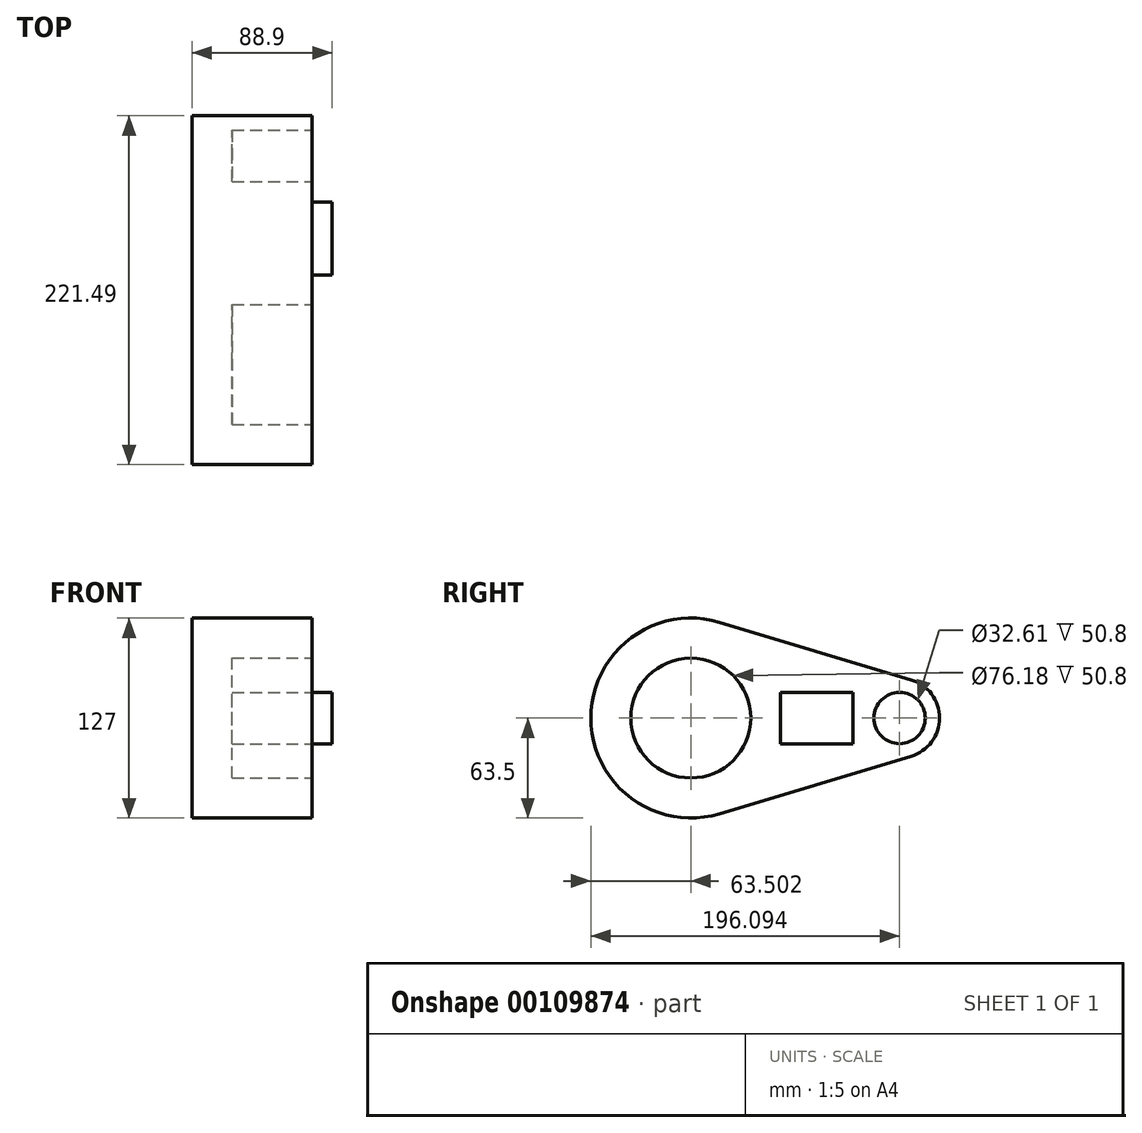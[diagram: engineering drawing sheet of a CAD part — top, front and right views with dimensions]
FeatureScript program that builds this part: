
annotation { "Feature Type Name" : "Feature", "Feature Type Description" : "" }
export const myFeature = defineFeature(function(context is Context, id is Id, definition is map)
    precondition{}
    {
        {
            var Q0;
            Q0=qCreatedBy(makeId("Right.planeOp"),FACE);
            var sketch = newSketch(context, id + "F0", { "sketchPlane" : qUnion([Q0])});
            skCircle(sketch, "E0", {"center": v(-79.97, 0) * mm, "radius": 63.5 * mm});
            skCircle(sketch, "E1", {"center": v(52.62, 0) * mm, "radius": 25.4 * mm});
            skLineSegment(sketch, "E2", {"start": v(-61.72, 60.82) * mm, "end": v(59.92, 24.33) * mm});
            skLineSegment(sketch, "E3", {"start": v(-61.72, -60.82) * mm, "end": v(59.92, -24.33) * mm});
            skSolve(sketch);
        }
        {
            var Q0;
            Q0 = qSketchRegion(id + "F0", true);
            extrude(context, id + "F1", {"entities" : qUnion([Q0]), "depth" : 76.2 * mm});
        }
        {
            var Q0;
            Q0=makeQuery(id+"F1.opExtrude","CAP_FACE",FACE,{"disambiguationData":[OSD([sQuery(id+"F0.wireOp",EDGE,"E0"),sQuery(id+"F0.wireOp",EDGE,"E1"),sQuery(id+"F0.wireOp",EDGE,"E2"),sQuery(id+"F0.wireOp",EDGE,"E3")])],"isStart":false});
            var sketch = newSketch(context, id + "F2", { "sketchPlane" : qUnion([Q0])});
            skCircle(sketch, "E4", {"center": v(-79.97, 0) * mm, "radius": 38.09 * mm});
            skCircle(sketch, "E5", {"center": v(52.62, 0) * mm, "radius": 16.3 * mm});
            skSolve(sketch);
        }
        {
            var Q0;
            Q0=makeQuery(id+"F2.imprint","IMPRINT",FACE,{"disambiguationData":[TD([[makeQuery(id+"F2.imprint","IMPRINT",EDGE,{"derivedFrom":sQuery(id+"F2.wireOp",EDGE,"E4")}),1.0]])]});
            var Q1;
            Q1=makeQuery(id+"F2.imprint","IMPRINT",FACE,{"disambiguationData":[TD([[makeQuery(id+"F2.imprint","IMPRINT",EDGE,{"derivedFrom":sQuery(id+"F2.wireOp",EDGE,"E5")}),1.0]])]});
            extrude(context, id + "F3", {"entities" : qUnion([Q0, Q1]), "operationType" : NewBodyOperationType.REMOVE, "oppositeDirection" : true, "depth" : 50.8 * mm});
        }
        {
            var Q0;
            Q0=makeQuery(id+"F1.opExtrude","CAP_FACE",FACE,{"disambiguationData":[OSD([sQuery(id+"F0.wireOp",EDGE,"E0"),sQuery(id+"F0.wireOp",EDGE,"E1"),sQuery(id+"F0.wireOp",EDGE,"E2"),sQuery(id+"F0.wireOp",EDGE,"E3")])],"isStart":false});
            var sketch = newSketch(context, id + "F4", { "sketchPlane" : qUnion([Q0])});
            skLineSegment(sketch, "E6.bottom", {"start": v(-23.1, 16.39) * mm, "end": v(23.1, 16.39) * mm});
            skLineSegment(sketch, "E6.top", {"start": v(-23.1, -16.39) * mm, "end": v(23.1, -16.39) * mm});
            skLineSegment(sketch, "E6.left", {"start": v(-23.1, 16.39) * mm, "end": v(-23.1, -16.39) * mm});
            skLineSegment(sketch, "E6.right", {"start": v(23.1, 16.39) * mm, "end": v(23.1, -16.39) * mm});
            skPoint(sketch, "E6.middle", {"position": v(0, 0) * mm});
            skSolve(sketch);
        }
        {
            var Q0;
            Q0=makeQuery(id+"F4.imprint","IMPRINT",FACE,{"disambiguationData":[TD([[makeQuery(id+"F4.imprint","IMPRINT",EDGE,{"derivedFrom":sQuery(id+"F4.wireOp",EDGE,"E6.bottom")}),-1.0]])]});
            extrude(context, id + "F5", {"entities" : qUnion([Q0]), "operationType" : NewBodyOperationType.ADD, "depth" : 12.7 * mm});
        }
    });
